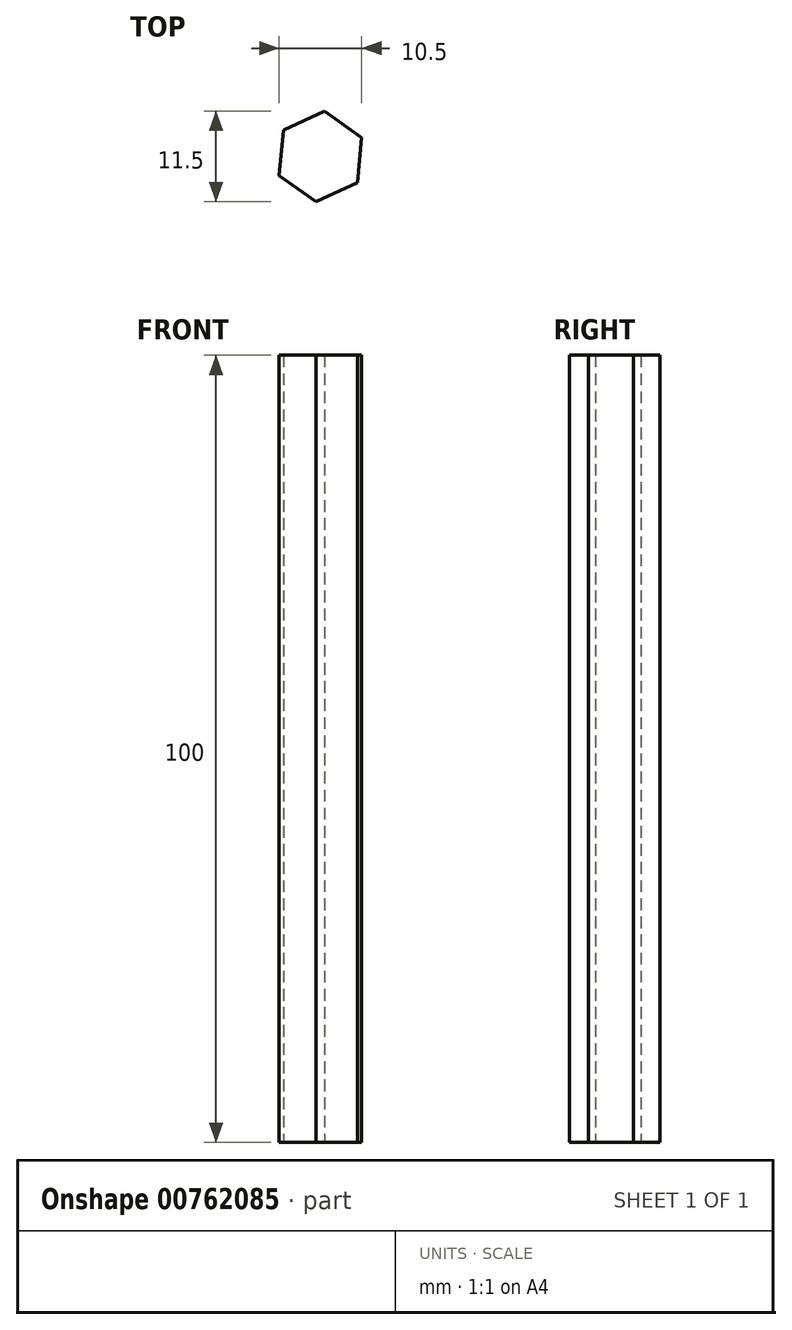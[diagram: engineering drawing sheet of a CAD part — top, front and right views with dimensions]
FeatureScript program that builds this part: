
annotation { "Feature Type Name" : "Feature", "Feature Type Description" : "" }
export const myFeature = defineFeature(function(context is Context, id is Id, definition is map)
    precondition{}
    {
        {
            var Q0;
            Q0=qCreatedBy(makeId("Top.planeOp"),FACE);
            var sketch = newSketch(context, id + "F0", { "sketchPlane" : qUnion([Q0])});
            skCircle(sketch, "E0.cCircle", {"center": v(0, 0) * mm, "radius": 5 * mm, "construction": true});
            skLineSegment(sketch, "E0.0", {"start": v(0.53, 5.75) * mm, "end": v(5.25, 2.41) * mm});
            skLineSegment(sketch, "E0.1", {"start": v(5.25, 2.41) * mm, "end": v(4.71, -3.34) * mm});
            skLineSegment(sketch, "E0.2", {"start": v(4.71, -3.34) * mm, "end": v(-0.53, -5.75) * mm});
            skLineSegment(sketch, "E0.3", {"start": v(-0.53, -5.75) * mm, "end": v(-5.25, -2.41) * mm});
            skLineSegment(sketch, "E0.4", {"start": v(-5.25, -2.41) * mm, "end": v(-4.71, 3.34) * mm});
            skLineSegment(sketch, "E0.5", {"start": v(-4.71, 3.34) * mm, "end": v(0.53, 5.75) * mm});
            skPoint(sketch, "E0.0.midPoint", {"position": v(2.89, 4.08) * mm});
            skSolve(sketch);
        }
        {
            var Q0;
            Q0 = qSketchRegion(id + "F0", true);
            extrude(context, id + "F1", {"entities" : qUnion([Q0]), "depth" : 100 * mm, "offsetDistance" : 25 * mm});
        }
    });
